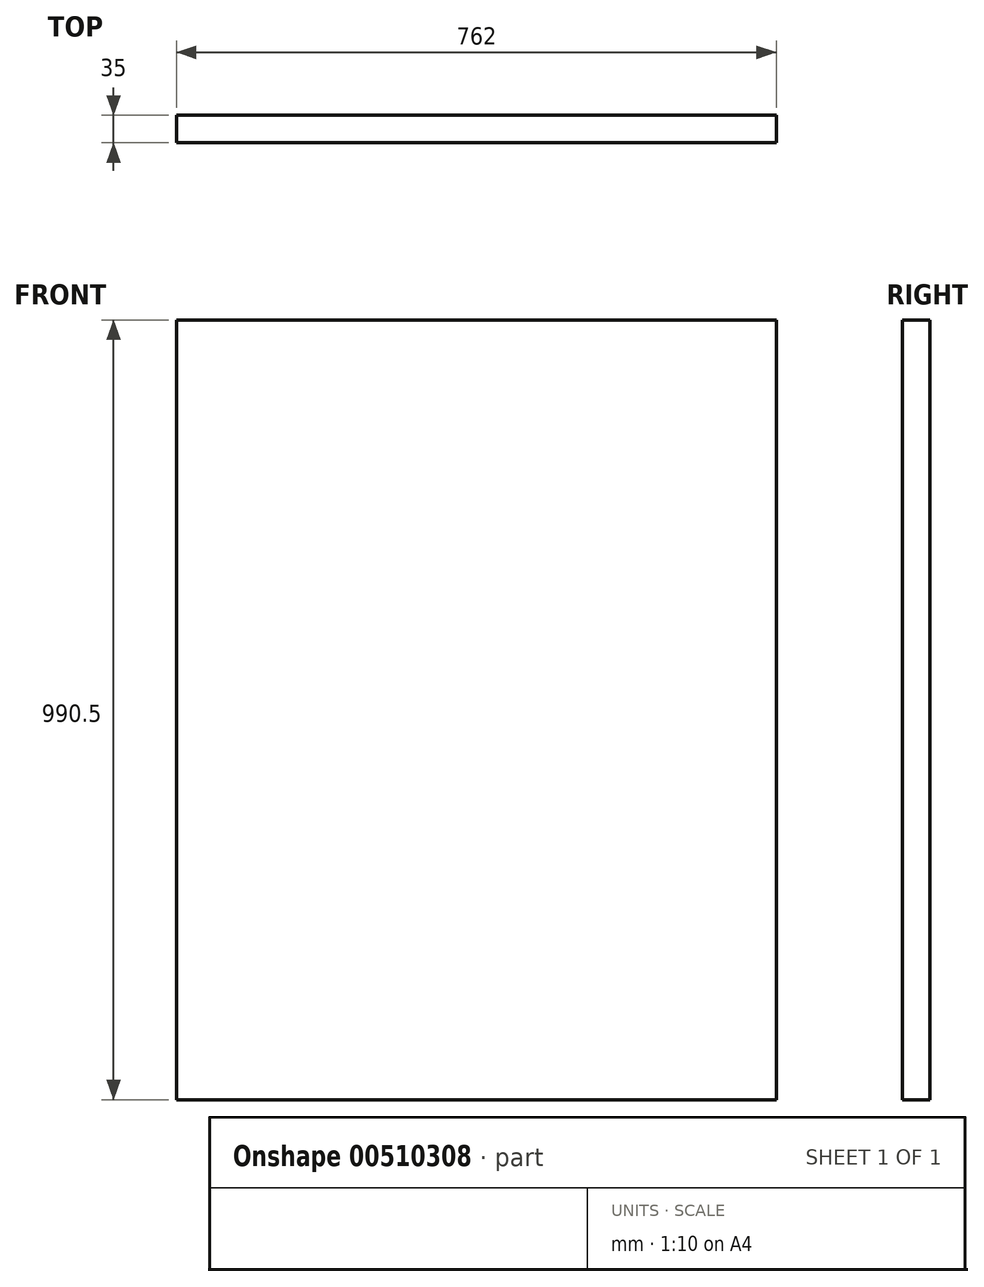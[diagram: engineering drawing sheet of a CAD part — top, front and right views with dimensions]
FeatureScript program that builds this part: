
annotation { "Feature Type Name" : "Feature", "Feature Type Description" : "" }
export const myFeature = defineFeature(function(context is Context, id is Id, definition is map)
    precondition{}
    {
        {
            var Q0;
            Q0=qCreatedBy(makeId("Front.planeOp"),FACE);
            var sketch = newSketch(context, id + "F0", { "sketchPlane" : qUnion([Q0])});
            skLineSegment(sketch, "E0.bottom", {"start": v(-558.1, 933.08) * mm, "end": v(203.9, 933.08) * mm});
            skLineSegment(sketch, "E0.top", {"start": v(-558.1, -1047.92) * mm, "end": v(203.9, -1047.92) * mm});
            skLineSegment(sketch, "E0.left", {"start": v(-558.1, 933.08) * mm, "end": v(-558.1, -1047.92) * mm});
            skLineSegment(sketch, "E0.right", {"start": v(203.9, 933.08) * mm, "end": v(203.9, -1047.92) * mm});
            skLineSegment(sketch, "E1", {"start": v(-558.1, -57.42) * mm, "end": v(203.9, -57.42) * mm});
            skSolve(sketch);
        }
        {
            var Q0;
            Q0=makeQuery(id+"F0.imprint","IMPRINT",FACE,{"disambiguationData":[TD([[makeQuery(id+"F0.imprint","IMPRINT",EDGE,{"derivedFrom":sQuery(id+"F0.wireOp",EDGE,"E0.bottom")}),-1.0]])]});
            extrude(context, id + "F1", {"entities" : qUnion([Q0]), "depth" : 35 * mm});
        }
    });
